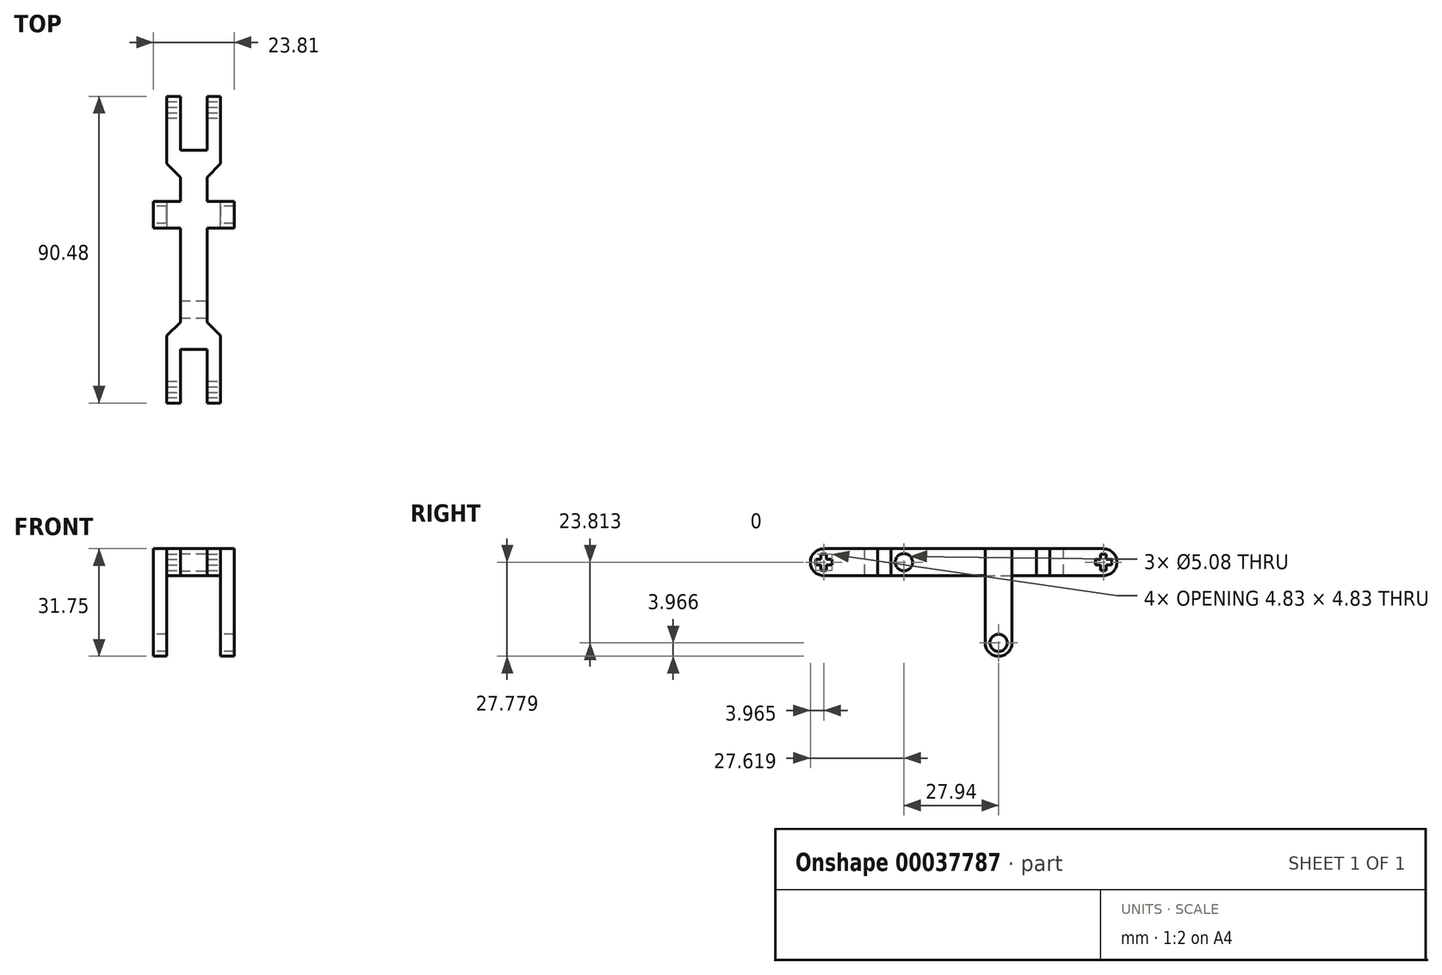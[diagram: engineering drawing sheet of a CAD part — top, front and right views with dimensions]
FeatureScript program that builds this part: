
annotation { "Feature Type Name" : "Feature", "Feature Type Description" : "" }
export const myFeature = defineFeature(function(context is Context, id is Id, definition is map)
    precondition{}
    {
        {
            var Q0;
            Q0=qCreatedBy(makeId("Top.planeOp"),FACE);
            var sketch = newSketch(context, id + "F0", { "sketchPlane" : qUnion([Q0])});
            skLineSegment(sketch, "E0.left", {"start": v(0, 0) * mm, "end": v(0, -19.84) * mm});
            skLineSegment(sketch, "E0.right", {"start": v(15.88, 0) * mm, "end": v(15.88, -19.84) * mm});
            skLineSegment(sketch, "E1", {"start": v(0, -19.84) * mm, "end": v(3.97, -19.84) * mm});
            skLineSegment(sketch, "E2", {"start": v(15.88, -19.84) * mm, "end": v(11.9, -19.84) * mm});
            skLineSegment(sketch, "E3.top", {"start": v(3.97, -3.97) * mm, "end": v(11.9, -3.97) * mm});
            skLineSegment(sketch, "E3.left", {"start": v(3.97, -19.84) * mm, "end": v(3.97, -3.97) * mm});
            skLineSegment(sketch, "E3.right", {"start": v(11.9, -19.84) * mm, "end": v(11.9, -3.97) * mm});
            skLineSegment(sketch, "E4", {"start": v(0, 0) * mm, "end": v(3.97, 0) * mm});
            skLineSegment(sketch, "E5", {"start": v(15.88, 0) * mm, "end": v(11.9, 0) * mm});
            skLineSegment(sketch, "E6", {"start": v(11.9, 0) * mm, "end": v(11.9, 50.8) * mm});
            skLineSegment(sketch, "E7", {"start": v(3.97, 50.8) * mm, "end": v(3.97, 0) * mm});
            skLineSegment(sketch, "E8", {"start": v(11.9, -3.97) * mm, "end": v(11.9, 0) * mm, "construction": true});
            skLineSegment(sketch, "E9", {"start": v(3.97, 50.8) * mm, "end": v(0, 50.8) * mm});
            skLineSegment(sketch, "E10", {"start": v(0, 50.8) * mm, "end": v(0, 70.64) * mm});
            skLineSegment(sketch, "E11", {"start": v(0, 70.64) * mm, "end": v(3.97, 70.64) * mm});
            skLineSegment(sketch, "E12", {"start": v(3.97, 70.64) * mm, "end": v(3.97, 54.77) * mm});
            skLineSegment(sketch, "E13", {"start": v(3.97, 54.77) * mm, "end": v(11.9, 54.77) * mm});
            skLineSegment(sketch, "E14", {"start": v(11.9, 54.77) * mm, "end": v(11.9, 70.64) * mm});
            skLineSegment(sketch, "E15", {"start": v(11.9, 70.64) * mm, "end": v(15.87, 70.64) * mm});
            skLineSegment(sketch, "E16", {"start": v(15.88, 70.64) * mm, "end": v(15.88, 50.8) * mm});
            skLineSegment(sketch, "E17", {"start": v(15.88, 50.8) * mm, "end": v(11.9, 50.8) * mm});
            skSolve(sketch);
        }
        {
            var Q0;
            Q0=qSketchRegion(id+"F0",true);
            extrude(context, id + "F1", {"entities" : qUnion([Q0]), "depth" : 7.94 * mm});
        }
        {
            var Q0;
            Q0=makeQuery(id+"F1.opExtrude","SWEPT_FACE",FACE,{"disambiguationData":[OSD([sQuery(id+"F0.wireOp",EDGE,"E0.right")])]});
            var sketch = newSketch(context, id + "F2", { "sketchPlane" : qUnion([Q0])});
            skLineSegment(sketch, "E18", {"start": v(-3.97, 7.94) * mm, "end": v(-15.88, 7.94) * mm});
            skLineSegment(sketch, "E19", {"start": v(-15.88, 0) * mm, "end": v(-3.97, 0) * mm});
            skArc(sketch, "E20", {"start": v(-15.88, 7.94) * mm, "mid": v(-19.84, 3.97) * mm, "end": v(-15.88, 0) * mm});
            skLineSegment(sketch, "E21.bottom", {"start": v(-3.97, 7.94) * mm, "end": v(-19.84, 7.94) * mm});
            skLineSegment(sketch, "E21.top", {"start": v(-3.97, 0) * mm, "end": v(-19.84, 0) * mm});
            skLineSegment(sketch, "E21.right", {"start": v(-19.84, 7.94) * mm, "end": v(-19.84, 0) * mm});
            skLineSegment(sketch, "E22", {"start": v(-15.88, 3.97) * mm, "end": v(7.78, 3.97) * mm, "construction": true});
            skCircle(sketch, "E23", {"center": v(7.78, 3.97) * mm, "radius": 2.54 * mm});
            skLineSegment(sketch, "E24.rect.bottom", {"start": v(-16.72, 6.38) * mm, "end": v(-15.03, 6.38) * mm});
            skLineSegment(sketch, "E24.rect.top", {"start": v(-16.72, 1.56) * mm, "end": v(-15.03, 1.56) * mm});
            skLineSegment(sketch, "E24.rect.left", {"start": v(-16.72, 6.38) * mm, "end": v(-16.72, 1.56) * mm});
            skLineSegment(sketch, "E24.rect.right", {"start": v(-15.03, 6.38) * mm, "end": v(-15.03, 1.56) * mm});
            skLineSegment(sketch, "E25.rect.bottom", {"start": v(-13.46, 4.81) * mm, "end": v(-18.29, 4.81) * mm});
            skLineSegment(sketch, "E25.rect.top", {"start": v(-13.46, 3.12) * mm, "end": v(-18.29, 3.12) * mm});
            skLineSegment(sketch, "E25.rect.left", {"start": v(-13.46, 4.81) * mm, "end": v(-13.46, 3.12) * mm});
            skLineSegment(sketch, "E25.rect.right", {"start": v(-18.29, 4.81) * mm, "end": v(-18.29, 3.12) * mm});
            skSolve(sketch);
        }
        {
            var Q0;
            Q0=qSketchRegion(id+"F2",true);
            var Q1;
            Q1=makeQuery(id+"F1.opExtrude","SWEPT_FACE",FACE,{"disambiguationData":[OSD([sQuery(id+"F0.wireOp",EDGE,"E0.left")])]});
            extrude(context, id + "F3", {"entities" : qUnion([Q0]), "operationType" : NewBodyOperationType.REMOVE, "endBound" : BoundingType.UP_TO_SURFACE, "oppositeDirection" : true, "endBoundEntityFace" : qUnion([Q1]), "depth" : 25.4 * mm});
        }
        {
            var Q0;
            Q0=makeQuery(id+"F1.opExtrude","SWEPT_EDGE",EDGE,{"disambiguationData":[OSD([sQuery(id+"F0.wireOp",EDGE,"E5"),sQuery(id+"F0.wireOp",EDGE,"E6")])]});
            var Q1;
            Q1=makeQuery(id+"F1.opExtrude","SWEPT_EDGE",EDGE,{"disambiguationData":[OSD([sQuery(id+"F0.wireOp",EDGE,"E4"),sQuery(id+"F0.wireOp",EDGE,"E7")])]});
            var Q2;
            Q2=makeQuery(id+"F1.opExtrude","SWEPT_EDGE",EDGE,{"disambiguationData":[OSD([sQuery(id+"F0.wireOp",EDGE,"E6"),sQuery(id+"F0.wireOp",EDGE,"E17")])]});
            var Q3;
            Q3=makeQuery(id+"F1.opExtrude","SWEPT_EDGE",EDGE,{"disambiguationData":[OSD([sQuery(id+"F0.wireOp",EDGE,"E7"),sQuery(id+"F0.wireOp",EDGE,"E9")])]});
            chamfer(context, id + "F4", {"entities" : qUnion([Q0, Q1, Q2, Q3]), "width" : 3.97 * mm, "tangentPropagation" : true});
        }
        {
            var Q0;
            Q0=makeQuery(id+"F1.opExtrude","CAP_FACE",FACE,{"disambiguationData":[OSD([sQuery(id+"F0.wireOp",EDGE,"E0.left"),sQuery(id+"F0.wireOp",EDGE,"E0.right"),sQuery(id+"F0.wireOp",EDGE,"E1"),sQuery(id+"F0.wireOp",EDGE,"E2"),sQuery(id+"F0.wireOp",EDGE,"E3.top"),sQuery(id+"F0.wireOp",EDGE,"E3.left"),sQuery(id+"F0.wireOp",EDGE,"E3.right"),sQuery(id+"F0.wireOp",EDGE,"E4"),sQuery(id+"F0.wireOp",EDGE,"E5"),sQuery(id+"F0.wireOp",EDGE,"E6"),sQuery(id+"F0.wireOp",EDGE,"94c80ab9-0a5f-4ac9-ab4e-fbbe913b1dfc"),sQuery(id+"F0.wireOp",EDGE,"E7")])],"isStart":false});
            var sketch = newSketch(context, id + "F5", { "sketchPlane" : qUnion([Q0])});
            skLineSegment(sketch, "E26.bottom", {"start": v(-3.97, 31.75) * mm, "end": v(3.97, 31.75) * mm});
            skLineSegment(sketch, "E26.top", {"start": v(-3.97, 39.69) * mm, "end": v(3.97, 39.69) * mm});
            skLineSegment(sketch, "E26.left", {"start": v(-3.97, 31.75) * mm, "end": v(-3.97, 39.69) * mm});
            skLineSegment(sketch, "E26.right", {"start": v(3.97, 31.75) * mm, "end": v(3.97, 39.69) * mm});
            skLineSegment(sketch, "E27.bottom", {"start": v(11.9, 31.75) * mm, "end": v(19.84, 31.75) * mm});
            skLineSegment(sketch, "E27.top", {"start": v(11.9, 39.69) * mm, "end": v(19.84, 39.69) * mm});
            skLineSegment(sketch, "E27.left", {"start": v(11.9, 31.75) * mm, "end": v(11.9, 39.69) * mm});
            skLineSegment(sketch, "E27.right", {"start": v(19.84, 31.75) * mm, "end": v(19.84, 39.69) * mm});
            skLineSegment(sketch, "E28", {"start": v(11.9, 35.72) * mm, "end": v(3.97, 35.72) * mm, "construction": true});
            skLineSegment(sketch, "E29", {"start": v(7.94, 35.72) * mm, "end": v(7.94, 54.77) * mm, "construction": true});
            skSolve(sketch);
        }
        {
            var Q0;
            Q0 = qSketchRegion(id + "F5", true);
            var Q1;
            Q1=makeQuery(id+"F1.opExtrude","CAP_FACE",FACE,{"disambiguationData":[OSD([sQuery(id+"F0.wireOp",EDGE,"E0.left"),sQuery(id+"F0.wireOp",EDGE,"E0.right"),sQuery(id+"F0.wireOp",EDGE,"E1"),sQuery(id+"F0.wireOp",EDGE,"E2"),sQuery(id+"F0.wireOp",EDGE,"E3.top"),sQuery(id+"F0.wireOp",EDGE,"E3.left"),sQuery(id+"F0.wireOp",EDGE,"E3.right"),sQuery(id+"F0.wireOp",EDGE,"E4"),sQuery(id+"F0.wireOp",EDGE,"E5"),sQuery(id+"F0.wireOp",EDGE,"E6"),sQuery(id+"F0.wireOp",EDGE,"94c80ab9-0a5f-4ac9-ab4e-fbbe913b1dfc"),sQuery(id+"F0.wireOp",EDGE,"E7")])],"isStart":true});
            extrude(context, id + "F6", {"entities" : qUnion([Q0]), "operationType" : NewBodyOperationType.ADD, "endBound" : BoundingType.UP_TO_SURFACE, "oppositeDirection" : true, "endBoundEntityFace" : qUnion([Q1]), "depth" : 25.4 * mm});
        }
        {
            var Q0;
            Q0=makeQuery(id+"F6.boolean.opBoolean","MERGE",FACE,{"derivedFrom":[makeQuery(id+"F1.opExtrude","CAP_FACE",FACE,{"disambiguationData":[OSD([sQuery(id+"F0.wireOp",EDGE,"E0.left"),sQuery(id+"F0.wireOp",EDGE,"E0.right"),sQuery(id+"F0.wireOp",EDGE,"E1"),sQuery(id+"F0.wireOp",EDGE,"E2"),sQuery(id+"F0.wireOp",EDGE,"E3.top"),sQuery(id+"F0.wireOp",EDGE,"E3.left"),sQuery(id+"F0.wireOp",EDGE,"E3.right"),sQuery(id+"F0.wireOp",EDGE,"E4"),sQuery(id+"F0.wireOp",EDGE,"E5"),sQuery(id+"F0.wireOp",EDGE,"E6"),sQuery(id+"F0.wireOp",EDGE,"94c80ab9-0a5f-4ac9-ab4e-fbbe913b1dfc"),sQuery(id+"F0.wireOp",EDGE,"E7")])],"isStart":true}),makeQuery(id+"F6.opExtrude","CAP_FACE",FACE,{"disambiguationData":[OSD([sQuery(id+"F5.wireOp",EDGE,"E26.bottom"),sQuery(id+"F5.wireOp",EDGE,"E26.top"),sQuery(id+"F5.wireOp",EDGE,"E26.left"),sQuery(id+"F5.wireOp",EDGE,"E26.right")])],"isStart":false}),makeQuery(id+"F6.opExtrude","CAP_FACE",FACE,{"disambiguationData":[OSD([sQuery(id+"F5.wireOp",EDGE,"E27.bottom"),sQuery(id+"F5.wireOp",EDGE,"E27.top"),sQuery(id+"F5.wireOp",EDGE,"E27.left"),sQuery(id+"F5.wireOp",EDGE,"E27.right")])],"isStart":false})]});
            var sketch = newSketch(context, id + "F7", { "sketchPlane" : qUnion([Q0])});
            skLineSegment(sketch, "E30.bottom", {"start": v(19.84, -31.75) * mm, "end": v(15.88, -31.75) * mm});
            skLineSegment(sketch, "E30.top", {"start": v(19.84, -39.69) * mm, "end": v(15.88, -39.69) * mm});
            skLineSegment(sketch, "E30.left", {"start": v(19.84, -31.75) * mm, "end": v(19.84, -39.69) * mm});
            skLineSegment(sketch, "E30.right", {"start": v(15.88, -31.75) * mm, "end": v(15.88, -39.69) * mm});
            skLineSegment(sketch, "E31.bottom", {"start": v(0, -39.69) * mm, "end": v(-3.97, -39.69) * mm});
            skLineSegment(sketch, "E31.top", {"start": v(0, -31.75) * mm, "end": v(-3.97, -31.75) * mm});
            skLineSegment(sketch, "E31.left", {"start": v(0, -39.69) * mm, "end": v(0, -31.75) * mm});
            skLineSegment(sketch, "E31.right", {"start": v(-3.97, -39.69) * mm, "end": v(-3.97, -31.75) * mm});
            skSolve(sketch);
        }
        {
            var Q0;
            Q0 = qSketchRegion(id + "F7", true);
            extrude(context, id + "F8", {"entities" : qUnion([Q0]), "operationType" : NewBodyOperationType.ADD, "depth" : 23.8 * mm});
        }
        {
            var Q0;
            Q0=makeQuery(id+"F8.opExtrude","CAP_EDGE",EDGE,{"disambiguationData":[OSD([sQuery(id+"F7.wireOp",EDGE,"E31.bottom")])],"isStart":false});
            var Q1;
            Q1=makeQuery(id+"F8.opExtrude","CAP_EDGE",EDGE,{"disambiguationData":[OSD([sQuery(id+"F7.wireOp",EDGE,"E31.top")])],"isStart":false});
            var Q2;
            Q2=makeQuery(id+"F8.opExtrude","CAP_EDGE",EDGE,{"disambiguationData":[OSD([sQuery(id+"F7.wireOp",EDGE,"E30.bottom")])],"isStart":false});
            var Q3;
            Q3=makeQuery(id+"F8.opExtrude","CAP_EDGE",EDGE,{"disambiguationData":[OSD([sQuery(id+"F7.wireOp",EDGE,"E30.top")])],"isStart":false});
            var Q4;
            Q4=makeQuery(id+"F1.opExtrude","CAP_EDGE",EDGE,{"disambiguationData":[OSD([sQuery(id+"F0.wireOp",EDGE,"E15")])],"isStart":true});
            var Q5;
            Q5=makeQuery(id+"F1.opExtrude","CAP_EDGE",EDGE,{"disambiguationData":[OSD([sQuery(id+"F0.wireOp",EDGE,"E15")])],"isStart":false});
            var Q6;
            Q6=makeQuery(id+"F1.opExtrude","CAP_EDGE",EDGE,{"disambiguationData":[OSD([sQuery(id+"F0.wireOp",EDGE,"E11")])],"isStart":false});
            var Q7;
            Q7=makeQuery(id+"F1.opExtrude","CAP_EDGE",EDGE,{"disambiguationData":[OSD([sQuery(id+"F0.wireOp",EDGE,"E11")])],"isStart":true});
            fillet(context, id + "F9", {"entities" : qUnion([Q0, Q1, Q2, Q3, Q4, Q5, Q6, Q7]), "radius" : 3.97 * mm, "tangentPropagation" : true, "allowEdgeOverflow" : false});
        }
        {
            var Q0;
            Q0=makeQuery(id+"F8.boolean.opBoolean","MERGE",FACE,{"derivedFrom":[makeQuery(id+"F6.opExtrude","SWEPT_FACE",FACE,{"disambiguationData":[OSD([sQuery(id+"F5.wireOp",EDGE,"E26.left")])]}),makeQuery(id+"F8.opExtrude","SWEPT_FACE",FACE,{"disambiguationData":[OSD([sQuery(id+"F7.wireOp",EDGE,"E31.right")])]})]});
            var sketch = newSketch(context, id + "F10", { "sketchPlane" : qUnion([Q0])});
            skCircle(sketch, "E32", {"center": v(-35.72, -19.84) * mm, "radius": 2.54 * mm});
            skSolve(sketch);
        }
        {
            var Q0;
            Q0 = qSketchRegion(id + "F10", true);
            var Q1;
            Q1=makeQuery(id+"F8.boolean.opBoolean","MERGE",FACE,{"derivedFrom":[makeQuery(id+"F6.opExtrude","SWEPT_FACE",FACE,{"disambiguationData":[OSD([sQuery(id+"F5.wireOp",EDGE,"E27.right")])]}),makeQuery(id+"F8.opExtrude","SWEPT_FACE",FACE,{"disambiguationData":[OSD([sQuery(id+"F7.wireOp",EDGE,"E30.left")])]})]});
            extrude(context, id + "F11", {"entities" : qUnion([Q0]), "operationType" : NewBodyOperationType.REMOVE, "endBound" : BoundingType.UP_TO_SURFACE, "oppositeDirection" : true, "endBoundEntityFace" : qUnion([Q1]), "depth" : 25.4 * mm});
        }
        {
            var Q0;
            Q0=makeQuery(id+"F1.opExtrude","SWEPT_FACE",FACE,{"disambiguationData":[OSD([sQuery(id+"F0.wireOp",EDGE,"E16")])]});
            var sketch = newSketch(context, id + "F12", { "sketchPlane" : qUnion([Q0])});
            skLineSegment(sketch, "E33.rect.bottom", {"start": v(65.83, 1.56) * mm, "end": v(67.52, 1.56) * mm});
            skLineSegment(sketch, "E33.rect.top", {"start": v(65.83, 6.38) * mm, "end": v(67.52, 6.38) * mm});
            skLineSegment(sketch, "E33.rect.left", {"start": v(65.83, 1.56) * mm, "end": v(65.83, 6.38) * mm});
            skLineSegment(sketch, "E33.rect.right", {"start": v(67.52, 1.56) * mm, "end": v(67.52, 6.38) * mm});
            skPoint(sketch, "E33.rect.middle", {"position": v(66.68, 3.97) * mm});
            skLineSegment(sketch, "E34.rect.bottom", {"start": v(64.26, 4.81) * mm, "end": v(69.09, 4.81) * mm});
            skLineSegment(sketch, "E34.rect.top", {"start": v(64.26, 3.12) * mm, "end": v(69.09, 3.12) * mm});
            skLineSegment(sketch, "E34.rect.left", {"start": v(64.26, 4.81) * mm, "end": v(64.26, 3.12) * mm});
            skLineSegment(sketch, "E34.rect.right", {"start": v(69.09, 4.81) * mm, "end": v(69.09, 3.12) * mm});
            skSolve(sketch);
        }
        {
            var Q0;
            Q0 = qSketchRegion(id + "F12", true);
            var Q1;
            Q1=makeQuery(id+"F1.opExtrude","SWEPT_FACE",FACE,{"disambiguationData":[OSD([sQuery(id+"F0.wireOp",EDGE,"E10")])]});
            extrude(context, id + "F13", {"entities" : qUnion([Q0]), "operationType" : NewBodyOperationType.REMOVE, "endBound" : BoundingType.UP_TO_SURFACE, "oppositeDirection" : true, "endBoundEntityFace" : qUnion([Q1]), "depth" : 25.4 * mm});
        }
    });
